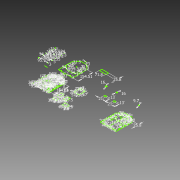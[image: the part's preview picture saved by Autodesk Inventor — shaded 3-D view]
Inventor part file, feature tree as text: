
AUTODESK INVENTOR PART (.ipt)
format: ipt  version: 2012 (Build 160160000, 160)  size: 351,232 bytes
history: native  units: mm
features: sketch x1
ambient origin geometry x8: Origin, YZ Plane, XZ Plane, XY Plane, X Axis, Y Axis, Z Axis, Center Point
feature tree (1):
  sketch  "Sketch1"  dims[d7=71.8mm d8=25.8mm d9=16.0mm d10=16.0mm d11=9.7mm d12=21.0mm d13=13.0mm d14=21.0mm d15=13.0mm d18=154.51mm d21=154.51mm d25=10.0mm d26=10.0mm d27=2.0mm d28=17.0mm d29=1.0mm d30=10.0mm d31=2.0mm d32=17.0mm d33=10.0mm d34=2.0mm d37=1.0mm d39=17.0mm d40=10.0mm d41=2.0mm d42=10.0mm d43=10.0mm d44=2.0mm d45=10.0mm d46=2.0mm d47=10.0mm d50=17.0mm d51=17.0mm d52=15.0mm d53=2.0mm d54=1.0mm d56=15.0mm d57=18.0mm d58=15.0mm d59=17.0mm d63=2.0mm d64=15.0mm d65=1.0mm d72=15.0mm d73=18.0mm d74=15.0mm d75=17.0mm d76=15.0mm d77=18.0mm d78=20.673333mm d80=20.836667mm d81=154.51mm d87=15.0mm d88=20.836667mm d92=18.0mm d93=219.764931mm d95=174.51mm d97=3.0mm d98=3.0mm d99=3.0mm d100=3.0mm d101=3.0mm d102=-5.117mm d103=10.0mm d104=15.117mm d105=10.0mm d106=5.554212mm d107=5.0mm d108=5.0mm d109=5.554212mm d110=5.554212mm d111=5.0mm d112=5.0mm d115=19.420788mm d116=60.018569mm d117=3.0mm d118=3.0mm d119=3.0mm d120=5.117mm d121=0.0mm d122=15.117007mm d123=3.0mm d124=5.0mm d125=5.0mm d126=5.0mm d127=5.000007mm d128=5.0mm d131=24.975mm d132=55.031431mm d133=60.0mm d134=25.0mm d135=30.0mm d136=3.0mm d137=12.5mm d138=57.0mm d139=67.0mm d140=3.0mm d141=3.0mm d142=3.0mm d143=51.0mm d144=51.0mm d145=51.0mm d146=51.0mm d147=3.0mm d151=2.0mm d152=12.0mm d153=12.0mm d154=11.0mm d155=11.0mm d156=3.0mm d157=3.0mm d158=3.0mm d159=2.0mm d160=12.0mm d161=12.0mm d162=14.0mm d163=11.0mm d164=154.51mm d168=3.0mm d169=8.0mm d170=8.0mm d171=3.0mm d172=8.0mm d173=8.0mm d176=10.0mm d177=2.0mm d180=10.0mm d181=2.0mm d183=10.0mm d184=2.0mm d187=10.0mm d188=2.0mm d189=10.0mm d190=10.0mm d191=2.0mm d192=10.0mm d193=2.0mm d194=10.0mm d197=15.0mm d198=2.0mm d200=15.0mm d201=18.0mm d202=15.0mm d203=17.0mm d204=2.0mm d205=15.0mm d207=15.0mm d208=18.0mm d209=15.0mm d210=17.0mm d211=15.0mm d212=18.0mm d216=15.0mm d219=18.0mm d220=219.764931mm d221=174.51mm d264=3.0mm d267=3.0mm d270=71.8mm d271=25.8mm d273=35.0mm d274=16.0mm d275=50.0mm d276=25.0mm d277=13.0mm d278=21.0mm d280=40.0mm d281=9.7mm d282=20.0mm d283=3.0mm d284=3.0mm d285=3.0mm d286=3.0mm d287=3.0mm d288=3.0mm d289=35.0mm d290=3.0mm d291=30.0mm d292=34.23504mm d293=34.23504mm d294=35.0mm d295=30.0mm d296=31.5mm d297=31.5mm d298=3.0mm d299=3.0mm d300=3.0mm d302=3.0mm d304=35.0mm d305=3.0mm d306=30.0mm d307=34.23504mm d308=34.23504mm d309=35.0mm d310=30.0mm d311=31.5mm d312=31.5mm d313=95.933639mm d314=95.933639mm d315=95.933639mm d316=95.933639mm d317=95.933639mm d318=95.933639mm d321=3.0mm d322=3.0mm d332=95.933639mm d335=95.933639mm d337=95.933639mm d339=50.0mm d341=25.0mm d342=30.0mm d343=60.0mm d344=5.0mm d345=110.0mm d346=20.0mm d347=55.0mm d349=10.0mm d350=5.0mm d351=28.5mm d352=44.6mm d353=3.0mm d354=3.0mm d355=2.2mm d356=23.7mm d357=2.2mm d358=39.8mm d359=32.7mm d360=45.5mm d361=2.6mm d362=2.6mm d363=27.4mm d364=40.4mm d365=44.6mm d366=28.5mm d367=3.0mm d368=3.0mm d369=2.2mm d370=2.2mm d371=23.7mm d372=39.8mm d373=45.5mm d374=32.7mm d375=3.0mm d376=3.0mm d377=2.6mm d378=2.6mm d379=27.4mm d380=40.4mm d385=27.4mm d386=40.4mm d391=3.0mm d392=3.0mm d394=23.7mm d396=39.8mm d399=30.0mm d400=30.0mm d401=5.0mm]
